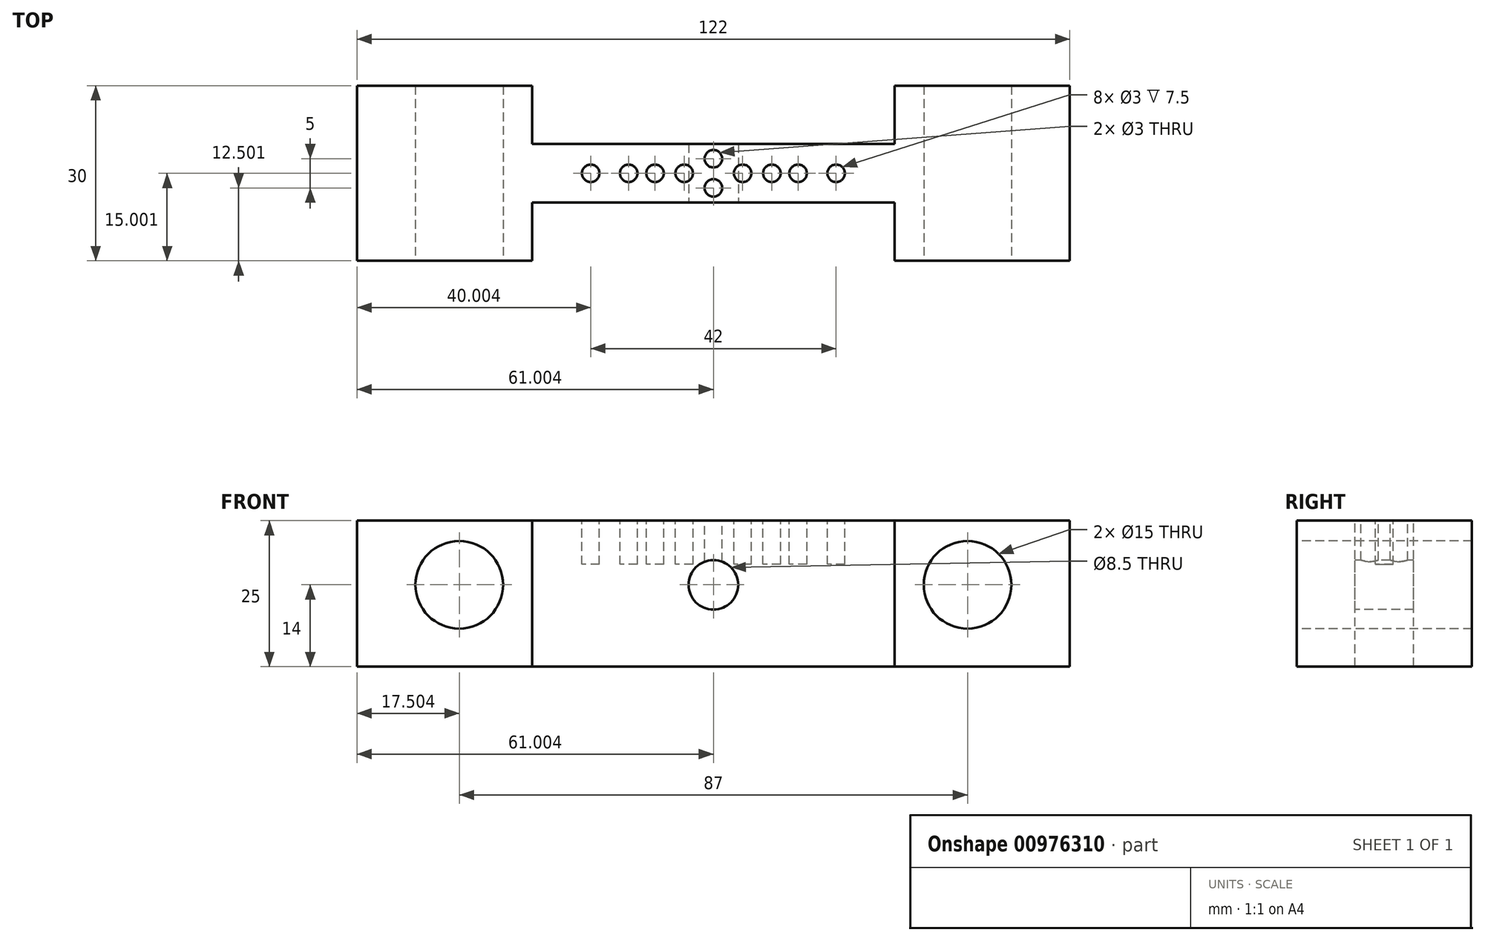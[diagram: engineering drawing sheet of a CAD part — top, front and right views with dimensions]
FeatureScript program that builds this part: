
annotation { "Feature Type Name" : "Feature", "Feature Type Description" : "" }
export const myFeature = defineFeature(function(context is Context, id is Id, definition is map)
    precondition{}
    {
        {
            var Q0;
            Q0=qCreatedBy(makeId("Top.planeOp"),FACE);
            var sketch = newSketch(context, id + "F0", { "sketchPlane" : qUnion([Q0])});
            skLineSegment(sketch, "E0.bottom", {"start": v(-54.63, -12.1) * mm, "end": v(67.37, -12.1) * mm});
            skLineSegment(sketch, "E0.top", {"start": v(-54.63, -42.1) * mm, "end": v(67.37, -42.1) * mm});
            skLineSegment(sketch, "E0.left", {"start": v(-54.63, -12.1) * mm, "end": v(-54.63, -42.1) * mm});
            skLineSegment(sketch, "E0.right", {"start": v(67.37, -12.1) * mm, "end": v(67.37, -42.1) * mm});
            skSolve(sketch);
        }
        {
            var Q0;
            Q0=makeQuery(id+"F0.imprint","IMPRINT",FACE,{"disambiguationData":[TD([[makeQuery(id+"F0.imprint","IMPRINT",EDGE,{"derivedFrom":sQuery(id+"F0.wireOp",EDGE,"E0.bottom")}),-1.0]])]});
            extrude(context, id + "F1", {"entities" : qUnion([Q0]), "depth" : 25 * mm, "offsetDistance" : 25 * mm});
        }
        {
            var Q0;
            Q0=makeQuery(id+"F1.opExtrude","SWEPT_FACE",FACE,{"disambiguationData":[OSD([sQuery(id+"F0.wireOp",EDGE,"E0.top")])]});
            var sketch = newSketch(context, id + "F2", { "sketchPlane" : qUnion([Q0])});
            skCircle(sketch, "E1", {"center": v(-37.13, 14) * mm, "radius": 7.5 * mm});
            skCircle(sketch, "E2", {"center": v(49.87, 14) * mm, "radius": 7.5 * mm});
            skCircle(sketch, "E3", {"center": v(6.37, 14) * mm, "radius": 4.25 * mm});
            skSolve(sketch);
        }
        {
            var Q0;
            Q0 = qSketchRegion(id + "F2", true);
            extrude(context, id + "F3", {"entities" : qUnion([Q0]), "operationType" : NewBodyOperationType.REMOVE, "endBound" : BoundingType.UP_TO_NEXT, "oppositeDirection" : true, "depth" : 25 * mm, "offsetDistance" : 25 * mm});
        }
        {
            var Q0;
            Q0=makeQuery(id+"F1.opExtrude","CAP_FACE",FACE,{"disambiguationData":[OSD([sQuery(id+"F0.wireOp",EDGE,"E0.bottom"),sQuery(id+"F0.wireOp",EDGE,"E0.top"),sQuery(id+"F0.wireOp",EDGE,"E0.left"),sQuery(id+"F0.wireOp",EDGE,"E0.right")])],"isStart":false});
            var sketch = newSketch(context, id + "F4", { "sketchPlane" : qUnion([Q0])});
            skLineSegment(sketch, "E4", {"start": v(-24.63, -42.1) * mm, "end": v(-24.63, -32.1) * mm});
            skLineSegment(sketch, "E5", {"start": v(-24.63, -32.1) * mm, "end": v(37.37, -32.1) * mm});
            skLineSegment(sketch, "E6", {"start": v(37.37, -32.1) * mm, "end": v(37.37, -42.1) * mm});
            skLineSegment(sketch, "E7", {"start": v(-24.63, -12.1) * mm, "end": v(-24.63, -22.1) * mm});
            skLineSegment(sketch, "E8", {"start": v(-24.63, -22.1) * mm, "end": v(37.37, -22.1) * mm});
            skLineSegment(sketch, "E9", {"start": v(37.37, -22.1) * mm, "end": v(37.37, -12.1) * mm});
            skSolve(sketch);
        }
        {
            var Q0;
            {var subQ0=sQuery(id+"F4.wireOp",EDGE,"E7");Q0=makeQuery(id+"F4.imprint","IMPRINT",FACE,{"disambiguationData":[TD([[makeQuery(id+"F4.imprint","IMPRINT",EDGE,{"derivedFrom":subQ0}),1.0]])]});}
            var Q1;
            {var subQ0=sQuery(id+"F4.wireOp",EDGE,"E4");Q1=makeQuery(id+"F4.imprint","IMPRINT",FACE,{"disambiguationData":[TD([[makeQuery(id+"F4.imprint","IMPRINT",EDGE,{"derivedFrom":subQ0}),-1.0]])]});}
            extrude(context, id + "F5", {"entities" : qUnion([Q0, Q1]), "operationType" : NewBodyOperationType.REMOVE, "oppositeDirection" : true, "depth" : 30 * mm, "offsetDistance" : 25 * mm});
        }
        {
            var Q0;
            Q0=makeQuery(id+"F1.opExtrude","CAP_FACE",FACE,{"disambiguationData":[OSD([sQuery(id+"F0.wireOp",EDGE,"E0.bottom"),sQuery(id+"F0.wireOp",EDGE,"E0.top"),sQuery(id+"F0.wireOp",EDGE,"E0.left"),sQuery(id+"F0.wireOp",EDGE,"E0.right")])],"isStart":false});
            var sketch = newSketch(context, id + "F6", { "sketchPlane" : qUnion([Q0])});
            skLineSegment(sketch, "E10", {"start": v(3.87, -22.1) * mm, "end": v(3.87, -32.1) * mm});
            skLineSegment(sketch, "E11", {"start": v(8.87, -22.1) * mm, "end": v(8.87, -32.1) * mm});
            skPoint(sketch, "E12.centerSnap0", {"position": v(6.37, -32.1) * mm});
            skCircle(sketch, "E13", {"center": v(11.37, -27.1) * mm, "radius": 1.5 * mm});
            skCircle(sketch, "E14", {"center": v(1.37, -27.1) * mm, "radius": 1.5 * mm});
            skCircle(sketch, "E15", {"center": v(16.37, -27.1) * mm, "radius": 1.5 * mm});
            skCircle(sketch, "E16", {"center": v(-3.63, -27.1) * mm, "radius": 1.5 * mm});
            skLineSegment(sketch, "E17", {"start": v(23.87, -22.1) * mm, "end": v(23.87, -32.1) * mm});
            skCircle(sketch, "E18", {"center": v(20.87, -27.1) * mm, "radius": 1.5 * mm});
            skCircle(sketch, "E19", {"center": v(-8.13, -27.1) * mm, "radius": 1.5 * mm});
            skCircle(sketch, "E20", {"center": v(27.37, -27.1) * mm, "radius": 1.5 * mm});
            skLineSegment(sketch, "E21", {"start": v(32.87, -22.1) * mm, "end": v(32.87, -32.1) * mm});
            skCircle(sketch, "E22", {"center": v(-14.63, -27.1) * mm, "radius": 1.5 * mm});
            skCircle(sketch, "E23", {"center": v(6.37, -24.6) * mm, "radius": 1.5 * mm});
            skCircle(sketch, "E24", {"center": v(6.37, -29.6) * mm, "radius": 1.5 * mm});
            skSolve(sketch);
        }
        {
            var Q0;
            Q0=makeQuery(id+"F6.imprint","IMPRINT",FACE,{"disambiguationData":[TD([[makeQuery(id+"F6.imprint","IMPRINT",EDGE,{"derivedFrom":sQuery(id+"F6.wireOp",EDGE,"E24")}),1.0]])]});
            var Q1;
            Q1=makeQuery(id+"F6.imprint","IMPRINT",FACE,{"disambiguationData":[TD([[makeQuery(id+"F6.imprint","IMPRINT",EDGE,{"derivedFrom":sQuery(id+"F6.wireOp",EDGE,"E23")}),1.0]])]});
            var Q2;
            Q2=makeQuery(id+"F6.imprint","IMPRINT",FACE,{"disambiguationData":[TD([[makeQuery(id+"F6.imprint","IMPRINT",EDGE,{"derivedFrom":sQuery(id+"F6.wireOp",EDGE,"E13")}),1.0]])]});
            var Q3;
            Q3=makeQuery(id+"F6.imprint","IMPRINT",FACE,{"disambiguationData":[TD([[makeQuery(id+"F6.imprint","IMPRINT",EDGE,{"derivedFrom":sQuery(id+"F6.wireOp",EDGE,"E15")}),1.0]])]});
            var Q4;
            Q4=makeQuery(id+"F6.imprint","IMPRINT",FACE,{"disambiguationData":[TD([[makeQuery(id+"F6.imprint","IMPRINT",EDGE,{"derivedFrom":sQuery(id+"F6.wireOp",EDGE,"E18")}),1.0]])]});
            var Q5;
            Q5=makeQuery(id+"F6.imprint","IMPRINT",FACE,{"disambiguationData":[TD([[makeQuery(id+"F6.imprint","IMPRINT",EDGE,{"derivedFrom":sQuery(id+"F6.wireOp",EDGE,"E20")}),1.0]])]});
            var Q6;
            Q6=makeQuery(id+"F6.imprint","IMPRINT",FACE,{"disambiguationData":[TD([[makeQuery(id+"F6.imprint","IMPRINT",EDGE,{"derivedFrom":sQuery(id+"F6.wireOp",EDGE,"E14")}),1.0]])]});
            var Q7;
            Q7=makeQuery(id+"F6.imprint","IMPRINT",FACE,{"disambiguationData":[TD([[makeQuery(id+"F6.imprint","IMPRINT",EDGE,{"derivedFrom":sQuery(id+"F6.wireOp",EDGE,"E16")}),1.0]])]});
            var Q8;
            Q8=makeQuery(id+"F6.imprint","IMPRINT",FACE,{"disambiguationData":[TD([[makeQuery(id+"F6.imprint","IMPRINT",EDGE,{"derivedFrom":sQuery(id+"F6.wireOp",EDGE,"E19")}),1.0]])]});
            var Q9;
            Q9=makeQuery(id+"F6.imprint","IMPRINT",FACE,{"disambiguationData":[TD([[makeQuery(id+"F6.imprint","IMPRINT",EDGE,{"derivedFrom":sQuery(id+"F6.wireOp",EDGE,"E22")}),1.0]])]});
            var Q10;
            Q10=sQuery(id+"F6.wireOp",EDGE,"E12");
            extrude(context, id + "F7", {"entities" : qUnion([Q0, Q1, Q2, Q3, Q4, Q5, Q6, Q7, Q8, Q9]), "operationType" : NewBodyOperationType.REMOVE, "surfaceEntities" : qUnion([Q10]), "oppositeDirection" : true, "depth" : 7.5 * mm, "offsetDistance" : 25 * mm});
        }
    });
